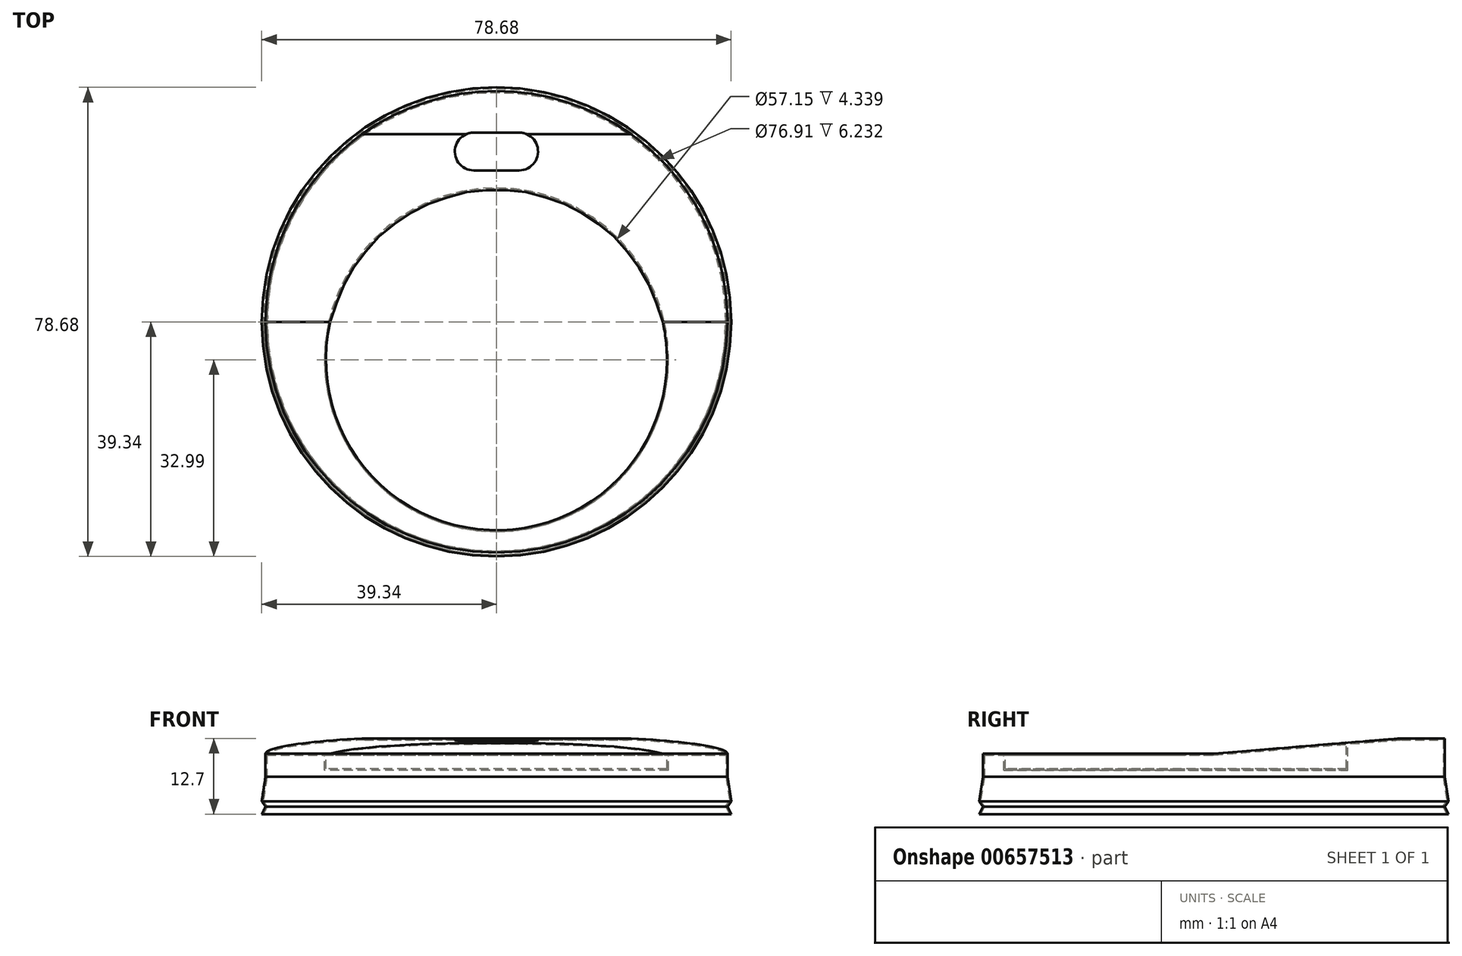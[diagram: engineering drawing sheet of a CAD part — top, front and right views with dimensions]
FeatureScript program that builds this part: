
annotation { "Feature Type Name" : "Feature", "Feature Type Description" : "" }
export const myFeature = defineFeature(function(context is Context, id is Id, definition is map)
    precondition{}
    {
        {
            var Q0;
            Q0=qCreatedBy(makeId("Top.planeOp"),FACE);
            var sketch = newSketch(context, id + "F0", { "sketchPlane" : qUnion([Q0])});
            skCircle(sketch, "E0", {"center": v(0, 0) * mm, "radius": 39.37 * mm});
            skSolve(sketch);
        }
        {
            var Q0;
            Q0=makeQuery(id+"F0.imprint","IMPRINT",FACE,{"disambiguationData":[TD([[makeQuery(id+"F0.imprint","IMPRINT",EDGE,{"derivedFrom":sQuery(id+"F0.wireOp",EDGE,"E0")}),1.0]])]});
            extrude(context, id + "F1", {"entities" : qUnion([Q0]), "depth" : 12.7 * mm, "offsetDistance" : 25.4 * mm});
        }
        {
            var Q0;
            Q0=makeQuery(id+"F1.opExtrude","CAP_FACE",FACE,{"disambiguationData":[OSD([sQuery(id+"F0.wireOp",EDGE,"E0")])],"isStart":false});
            var sketch = newSketch(context, id + "F2", { "sketchPlane" : qUnion([Q0])});
            skCircle(sketch, "E1", {"center": v(0, -6.35) * mm, "radius": 28.58 * mm});
            skSolve(sketch);
        }
        {
            var Q0;
            Q0=makeQuery(id+"F2.imprint","IMPRINT",FACE,{"disambiguationData":[TD([[makeQuery(id+"F2.imprint","IMPRINT",EDGE,{"derivedFrom":sQuery(id+"F2.wireOp",EDGE,"E1")}),1.0]])]});
            extrude(context, id + "F3", {"entities" : qUnion([Q0]), "operationType" : NewBodyOperationType.REMOVE, "oppositeDirection" : true, "depth" : 5.08 * mm, "offsetDistance" : 25.4 * mm});
        }
        {
            var Q0;
            Q0=qCreatedBy(makeId("Right.planeOp"),FACE);
            var sketch = newSketch(context, id + "F4", { "sketchPlane" : qUnion([Q0])});
            skLineSegment(sketch, "E2", {"start": v(31.48, 12.7) * mm, "end": v(0, 10.16) * mm});
            skLineSegment(sketch, "E3", {"start": v(0, 10.16) * mm, "end": v(-39.37, 10.16) * mm});
            skLineSegment(sketch, "E4", {"start": v(-39.37, 10.16) * mm, "end": v(-39.37, 13.75) * mm});
            skLineSegment(sketch, "E5", {"start": v(-39.37, 13.75) * mm, "end": v(31.48, 12.7) * mm});
            skSolve(sketch);
        }
        {
            var Q0;
            Q0 = qSketchRegion(id + "F4", true);
            extrude(context, id + "F5", {"entities" : qUnion([Q0]), "operationType" : NewBodyOperationType.REMOVE, "endBound" : BoundingType.THROUGH_ALL, "oppositeDirection" : true, "depth" : 25.4 * mm, "offsetDistance" : 25.4 * mm, "hasSecondDirection" : true, "secondDirectionBound" : SecondDirectionBoundingType.THROUGH_ALL, "secondDirectionOppositeDirection" : false, "secondDirectionDepth" : 25.4 * mm});
        }
        {
            var Q0;
            Q0=qCreatedBy(makeId("Right.planeOp"),FACE);
            var sketch = newSketch(context, id + "F6", { "sketchPlane" : qUnion([Q0])});
            skLineSegment(sketch, "E6", {"start": v(-39.34, 0) * mm, "end": v(-38.7, 1.27) * mm});
            skLineSegment(sketch, "E7", {"start": v(-38.7, 1.27) * mm, "end": v(-39.34, 2.14) * mm});
            skLineSegment(sketch, "E8", {"start": v(-39.34, 2.14) * mm, "end": v(-38.7, 6.23) * mm});
            skLineSegment(sketch, "E9", {"start": v(-38.7, 6.23) * mm, "end": v(-38.7, 17.29) * mm});
            skLineSegment(sketch, "E10", {"start": v(-38.7, 17.29) * mm, "end": v(-40.21, 17.29) * mm});
            skLineSegment(sketch, "E11", {"start": v(-40.21, 17.29) * mm, "end": v(-40.4, 0) * mm});
            skLineSegment(sketch, "E12", {"start": v(-40.4, 0) * mm, "end": v(-39.34, 0) * mm});
            skSolve(sketch);
        }
        {
            var Q0;
            Q0=makeQuery(id+"F6.imprint","IMPRINT",FACE,{"disambiguationData":[TD([[makeQuery(id+"F6.imprint","IMPRINT",EDGE,{"derivedFrom":sQuery(id+"F6.wireOp",EDGE,"E6")}),1.0]])]});
            var Q1;
            Q1=makeQuery(id+"F1.opExtrude","SWEPT_FACE",FACE,{"disambiguationData":[OSD([sQuery(id+"F0.wireOp",EDGE,"E0")])]});
            revolve(context, id + "F7", {"operationType" : NewBodyOperationType.REMOVE, "entities" : qUnion([Q0]), "axis" : qUnion([Q1]), "revolveType" : RevolveType.FULL, "oppositeDirection" : true});
        }
        {
            var Q0;
            Q0=makeQuery(id+"F1.opExtrude","CAP_FACE",FACE,{"disambiguationData":[OSD([sQuery(id+"F0.wireOp",EDGE,"E0")])],"isStart":true});
            shell(context, id + "F8", {"entities" : qUnion([Q0]), "thickness" : 0.25 * mm});
        }
        {
            var Q0;
            Q0=qCreatedBy(makeId("Top.planeOp"),FACE);
            var sketch = newSketch(context, id + "F9", { "sketchPlane" : qUnion([Q0])});
            skCircle(sketch, "E13", {"center": v(-3.81, 28.58) * mm, "radius": 3.18 * mm});
            skCircle(sketch, "E14", {"center": v(3.8, 28.58) * mm, "radius": 3.18 * mm});
            skLineSegment(sketch, "E15", {"start": v(3.8, 31.75) * mm, "end": v(-3.81, 31.75) * mm});
            skLineSegment(sketch, "E16", {"start": v(-3.81, 25.4) * mm, "end": v(3.8, 25.4) * mm});
            skSolve(sketch);
        }
        {
            var Q0;
            Q0 = qSketchRegion(id + "F9", true);
            extrude(context, id + "F10", {"entities" : qUnion([Q0]), "operationType" : NewBodyOperationType.REMOVE, "endBound" : BoundingType.THROUGH_ALL, "depth" : 25.4 * mm, "offsetDistance" : 25.4 * mm});
        }
    });
